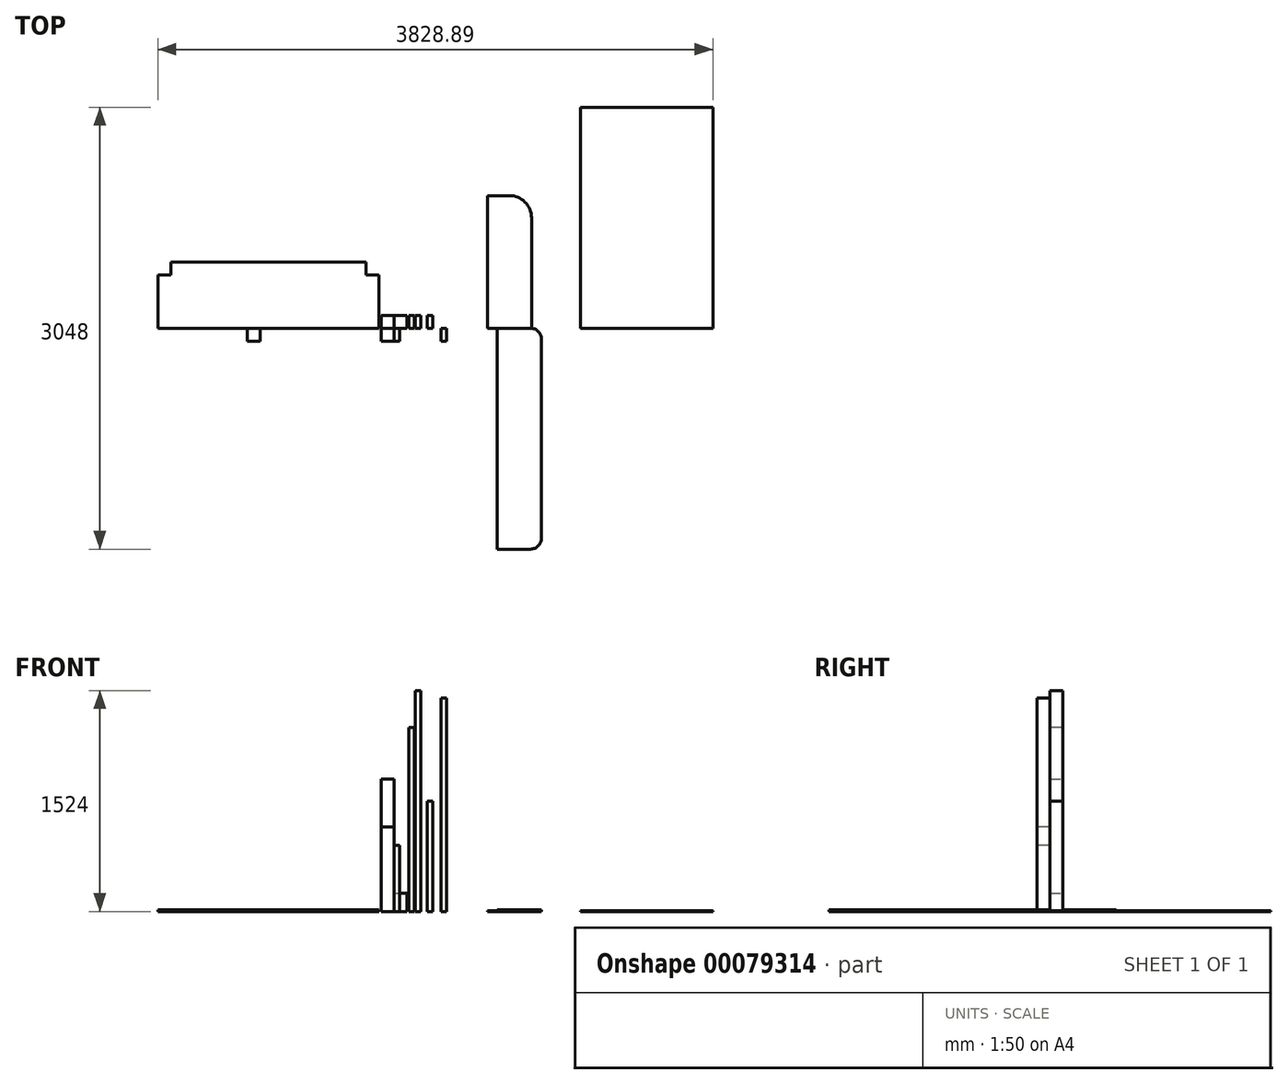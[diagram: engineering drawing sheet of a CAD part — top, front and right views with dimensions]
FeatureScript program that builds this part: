
annotation { "Feature Type Name" : "Feature", "Feature Type Description" : "" }
export const myFeature = defineFeature(function(context is Context, id is Id, definition is map)
    precondition{}
    {
        {
            var Q0;
            Q0=qCreatedBy(makeId("Top.planeOp"),FACE);
            var sketch = newSketch(context, id + "F0", { "sketchPlane" : qUnion([Q0])});
            skLineSegment(sketch, "E0.bottom", {"start": v(0, 0) * mm, "end": v(38.1, 0) * mm});
            skLineSegment(sketch, "E0.top", {"start": v(0, -88.9) * mm, "end": v(38.1, -88.9) * mm});
            skLineSegment(sketch, "E0.left", {"start": v(0, 0) * mm, "end": v(0, -88.9) * mm});
            skLineSegment(sketch, "E0.right", {"start": v(38.1, 0) * mm, "end": v(38.1, -88.9) * mm});
            skSolve(sketch);
        }
        {
            var Q0;
            Q0=qCreatedBy(makeId("Top.planeOp"),FACE);
            var sketch = newSketch(context, id + "F1", { "sketchPlane" : qUnion([Q0])});
            skLineSegment(sketch, "E1.bottom", {"start": v(0, 0) * mm, "end": v(-88.9, 0) * mm});
            skLineSegment(sketch, "E1.top", {"start": v(0, 88.9) * mm, "end": v(-88.9, 88.9) * mm});
            skLineSegment(sketch, "E1.left", {"start": v(0, 0) * mm, "end": v(0, 88.9) * mm});
            skLineSegment(sketch, "E1.right", {"start": v(-88.9, 0) * mm, "end": v(-88.9, 88.9) * mm});
            skSolve(sketch);
        }
        {
            var Q0;
            Q0=makeQuery(id+"F0.imprint","IMPRINT",FACE,{"disambiguationData":[TD([[makeQuery(id+"F0.imprint","IMPRINT",EDGE,{"derivedFrom":sQuery(id+"F0.wireOp",EDGE,"E0.bottom")}),-1.0]])]});
            extrude(context, id + "F2", {"entities" : qUnion([Q0]), "depth" : 457.2 * mm});
        }
        {
            var Q0;
            Q0=makeQuery(id+"F1.imprint","IMPRINT",FACE,{"disambiguationData":[TD([[makeQuery(id+"F1.imprint","IMPRINT",EDGE,{"derivedFrom":sQuery(id+"F1.wireOp",EDGE,"E1.bottom")}),-1.0]])]});
            extrude(context, id + "F3", {"entities" : qUnion([Q0]), "depth" : 914.4 * mm});
        }
        {
            var Q0;
            Q0=qCreatedBy(makeId("Top.planeOp"),FACE);
            var sketch = newSketch(context, id + "F4", { "sketchPlane" : qUnion([Q0])});
            skLineSegment(sketch, "E2.bottom", {"start": v(0, 0) * mm, "end": v(88.9, 0) * mm});
            skLineSegment(sketch, "E2.top", {"start": v(0, 88.9) * mm, "end": v(88.9, 88.9) * mm});
            skLineSegment(sketch, "E2.left", {"start": v(0, 0) * mm, "end": v(0, 88.9) * mm});
            skLineSegment(sketch, "E2.right", {"start": v(88.9, 0) * mm, "end": v(88.9, 88.9) * mm});
            skSolve(sketch);
        }
        {
            var Q0;
            Q0=qCreatedBy(makeId("Top.planeOp"),FACE);
            var sketch = newSketch(context, id + "F5", { "sketchPlane" : qUnion([Q0])});
            skLineSegment(sketch, "E3.bottom", {"start": v(0, 0) * mm, "end": v(-88.9, 0) * mm});
            skLineSegment(sketch, "E3.top", {"start": v(0, -88.9) * mm, "end": v(-88.9, -88.9) * mm});
            skLineSegment(sketch, "E3.left", {"start": v(0, 0) * mm, "end": v(0, -88.9) * mm});
            skLineSegment(sketch, "E3.right", {"start": v(-88.9, 0) * mm, "end": v(-88.9, -88.9) * mm});
            skSolve(sketch);
        }
        {
            var Q0;
            Q0=makeQuery(id+"F4.imprint","IMPRINT",FACE,{"disambiguationData":[TD([[makeQuery(id+"F4.imprint","IMPRINT",EDGE,{"derivedFrom":sQuery(id+"F4.wireOp",EDGE,"E2.bottom")}),1.0]])]});
            extrude(context, id + "F6", {"entities" : qUnion([Q0]), "depth" : 127 * mm});
        }
        {
            var Q0;
            Q0=makeQuery(id+"F5.imprint","IMPRINT",FACE,{"disambiguationData":[TD([[makeQuery(id+"F5.imprint","IMPRINT",EDGE,{"derivedFrom":sQuery(id+"F5.wireOp",EDGE,"E3.bottom")}),1.0]])]});
            extrude(context, id + "F7", {"entities" : qUnion([Q0]), "depth" : 584.2 * mm});
        }
        {
            var Q0;
            Q0=qCreatedBy(makeId("Top.planeOp"),FACE);
            var sketch = newSketch(context, id + "F8", { "sketchPlane" : qUnion([Q0])});
            skLineSegment(sketch, "E4.bottom", {"start": v(140.51, 88.9) * mm, "end": v(102.41, 88.9) * mm});
            skLineSegment(sketch, "E4.top", {"start": v(140.51, 0) * mm, "end": v(102.41, 0) * mm});
            skLineSegment(sketch, "E4.left", {"start": v(140.51, 88.9) * mm, "end": v(140.51, 0) * mm});
            skLineSegment(sketch, "E4.right", {"start": v(102.41, 88.9) * mm, "end": v(102.41, 0) * mm});
            skSolve(sketch);
        }
        {
            var Q0;
            Q0=makeQuery(id+"F8.imprint","IMPRINT",FACE,{"disambiguationData":[TD([[makeQuery(id+"F8.imprint","IMPRINT",EDGE,{"derivedFrom":sQuery(id+"F8.wireOp",EDGE,"E4.bottom")}),1.0]])]});
            extrude(context, id + "F9", {"entities" : qUnion([Q0]), "depth" : 1270 * mm});
        }
        {
            var Q0;
            Q0=qCreatedBy(makeId("Top.planeOp"),FACE);
            var sketch = newSketch(context, id + "F10", { "sketchPlane" : qUnion([Q0])});
            skLineSegment(sketch, "E5.bottom", {"start": v(183.48, 0) * mm, "end": v(145.38, 0) * mm});
            skLineSegment(sketch, "E5.top", {"start": v(183.48, 88.9) * mm, "end": v(145.38, 88.9) * mm});
            skLineSegment(sketch, "E5.left", {"start": v(183.48, 0) * mm, "end": v(183.48, 88.9) * mm});
            skLineSegment(sketch, "E5.right", {"start": v(145.38, 0) * mm, "end": v(145.38, 88.9) * mm});
            skSolve(sketch);
        }
        {
            var Q0;
            Q0=makeQuery(id+"F10.imprint","IMPRINT",FACE,{"disambiguationData":[TD([[makeQuery(id+"F10.imprint","IMPRINT",EDGE,{"derivedFrom":sQuery(id+"F10.wireOp",EDGE,"E5.bottom")}),-1.0]])]});
            extrude(context, id + "F11", {"entities" : qUnion([Q0]), "depth" : 1524 * mm});
        }
        {
            var Q0;
            Q0=qCreatedBy(makeId("Top.planeOp"),FACE);
            var sketch = newSketch(context, id + "F12", { "sketchPlane" : qUnion([Q0])});
            skLineSegment(sketch, "E6.bottom", {"start": v(267.37, 88.9) * mm, "end": v(229.27, 88.9) * mm});
            skLineSegment(sketch, "E6.top", {"start": v(267.37, 0) * mm, "end": v(229.27, 0) * mm});
            skLineSegment(sketch, "E6.left", {"start": v(267.37, 88.9) * mm, "end": v(267.37, 0) * mm});
            skLineSegment(sketch, "E6.right", {"start": v(229.27, 88.9) * mm, "end": v(229.27, 0) * mm});
            skSolve(sketch);
        }
        {
            var Q0;
            Q0=makeQuery(id+"F12.imprint","IMPRINT",FACE,{"disambiguationData":[TD([[makeQuery(id+"F12.imprint","IMPRINT",EDGE,{"derivedFrom":sQuery(id+"F12.wireOp",EDGE,"E6.bottom")}),1.0]])]});
            extrude(context, id + "F13", {"entities" : qUnion([Q0]), "depth" : 762 * mm});
        }
        {
            var Q0;
            Q0=qCreatedBy(makeId("Top.planeOp"),FACE);
            var sketch = newSketch(context, id + "F14", { "sketchPlane" : qUnion([Q0])});
            skLineSegment(sketch, "E7.bottom", {"start": v(-106.42, 0) * mm, "end": v(-1630.42, 0) * mm});
            skLineSegment(sketch, "E7.top", {"start": v(-106.42, 457.2) * mm, "end": v(-1630.42, 457.2) * mm});
            skLineSegment(sketch, "E7.left", {"start": v(-106.42, 0) * mm, "end": v(-106.42, 457.2) * mm});
            skLineSegment(sketch, "E7.right", {"start": v(-1630.42, 0) * mm, "end": v(-1630.42, 457.2) * mm});
            skLineSegment(sketch, "E8.bottom", {"start": v(-106.42, 457.2) * mm, "end": v(-195.32, 457.2) * mm});
            skLineSegment(sketch, "E8.top", {"start": v(-106.42, 368.3) * mm, "end": v(-195.32, 368.3) * mm});
            skLineSegment(sketch, "E8.left", {"start": v(-106.42, 457.2) * mm, "end": v(-106.42, 368.3) * mm});
            skLineSegment(sketch, "E8.right", {"start": v(-195.32, 457.2) * mm, "end": v(-195.32, 368.3) * mm});
            skLineSegment(sketch, "E9.top", {"start": v(-1630.42, 368.3) * mm, "end": v(-1541.52, 368.3) * mm});
            skLineSegment(sketch, "E9.left", {"start": v(-1630.42, 457.2) * mm, "end": v(-1630.42, 368.3) * mm});
            skLineSegment(sketch, "E9.right", {"start": v(-1541.52, 457.2) * mm, "end": v(-1541.52, 368.3) * mm});
            skSolve(sketch);
        }
        {
            var Q0;
            Q0=makeQuery(id+"F14.imprint","IMPRINT",FACE,{"disambiguationData":[TD([[makeQuery(id+"F14.imprint","IMPRINT",EDGE,{"derivedFrom":sQuery(id+"F14.wireOp",EDGE,"E7.bottom")}),-1.0]])]});
            extrude(context, id + "F15", {"entities" : qUnion([Q0]), "depth" : 12.7 * mm});
        }
        {
            var Q0;
            Q0=qCreatedBy(makeId("Top.planeOp"),FACE);
            var sketch = newSketch(context, id + "F16", { "sketchPlane" : qUnion([Q0])});
            skLineSegment(sketch, "E10.bottom", {"start": v(-125.56, 0) * mm, "end": v(-1014.56, 0) * mm});
            skLineSegment(sketch, "E10.top", {"start": v(-125.56, -457.2) * mm, "end": v(-1014.56, -457.2) * mm});
            skLineSegment(sketch, "E10.left", {"start": v(-125.56, 0) * mm, "end": v(-125.56, -457.2) * mm});
            skLineSegment(sketch, "E10.right", {"start": v(-1014.56, 0) * mm, "end": v(-1014.56, -457.2) * mm});
            skLineSegment(sketch, "E11.bottom", {"start": v(-1014.56, 0) * mm, "end": v(-925.66, 0) * mm});
            skLineSegment(sketch, "E11.top", {"start": v(-1014.56, -88.9) * mm, "end": v(-925.66, -88.9) * mm});
            skLineSegment(sketch, "E11.left", {"start": v(-1014.56, 0) * mm, "end": v(-1014.56, -88.9) * mm});
            skLineSegment(sketch, "E11.right", {"start": v(-925.66, 0) * mm, "end": v(-925.66, -88.9) * mm});
            skLineSegment(sketch, "E12.bottom", {"start": v(-1014.56, -457.2) * mm, "end": v(-925.66, -457.2) * mm});
            skLineSegment(sketch, "E12.top", {"start": v(-1014.56, -368.3) * mm, "end": v(-925.66, -368.3) * mm});
            skLineSegment(sketch, "E12.left", {"start": v(-1014.56, -457.2) * mm, "end": v(-1014.56, -368.3) * mm});
            skLineSegment(sketch, "E12.right", {"start": v(-925.66, -457.2) * mm, "end": v(-925.66, -368.3) * mm});
            skSolve(sketch);
        }
        {
            var Q0;
            Q0=makeQuery(id+"F16.imprint","IMPRINT",FACE,{"disambiguationData":[TD([[makeQuery(id+"F16.imprint","IMPRINT",EDGE,{"derivedFrom":sQuery(id+"F16.wireOp",EDGE,"E10.bottom")}),1.0]])]});
            extrude(context, id + "F17", {"entities" : qUnion([Q0]), "depth" : 12.7 * mm});
        }
        {
            var Q0;
            Q0=qCreatedBy(makeId("Top.planeOp"),FACE);
            var sketch = newSketch(context, id + "F18", { "sketchPlane" : qUnion([Q0])});
            skLineSegment(sketch, "E13.bottom", {"start": v(939.93, 0) * mm, "end": v(711.33, 0) * mm});
            skLineSegment(sketch, "E13.top", {"start": v(939.93, -1524) * mm, "end": v(711.33, -1524) * mm});
            skLineSegment(sketch, "E13.left", {"start": v(1016.13, -76.2) * mm, "end": v(1016.13, -1447.8) * mm});
            skLineSegment(sketch, "E13.right", {"start": v(711.33, 0) * mm, "end": v(711.33, -1524) * mm});
            skPoint(sketch, "E14.visualSharp", {"position": v(1016.13, 0) * mm});
            skArc(sketch, "E14.filletArc", {"start": v(1016.13, -76.2) * mm, "mid": v(993.82, -22.32) * mm, "end": v(939.93, 0) * mm});
            skPoint(sketch, "E15.visualSharp", {"position": v(1016.13, -1524) * mm});
            skArc(sketch, "E15.filletArc", {"start": v(939.93, -1524) * mm, "mid": v(993.82, -1501.68) * mm, "end": v(1016.13, -1447.8) * mm});
            skSolve(sketch);
        }
        {
            var Q0;
            Q0=makeQuery(id+"F18.imprint","IMPRINT",FACE,{"disambiguationData":[TD([[makeQuery(id+"F18.imprint","IMPRINT",EDGE,{"derivedFrom":sQuery(id+"F18.wireOp",EDGE,"E13.bottom")}),1.0]])]});
            extrude(context, id + "F19", {"entities" : qUnion([Q0]), "depth" : 12.7 * mm});
        }
        {
            var Q0;
            Q0=qCreatedBy(makeId("Top.planeOp"),FACE);
            var sketch = newSketch(context, id + "F20", { "sketchPlane" : qUnion([Q0])});
            skLineSegment(sketch, "E16.bottom", {"start": v(642.44, 0) * mm, "end": v(947.24, 0) * mm});
            skLineSegment(sketch, "E16.top", {"start": v(642.44, 914.4) * mm, "end": v(794.84, 914.4) * mm});
            skLineSegment(sketch, "E16.left", {"start": v(642.44, 0) * mm, "end": v(642.44, 914.4) * mm});
            skLineSegment(sketch, "E16.right", {"start": v(947.24, 0) * mm, "end": v(947.24, 762) * mm});
            skPoint(sketch, "E17.visualSharp", {"position": v(947.24, 914.4) * mm});
            skArc(sketch, "E17.filletArc", {"start": v(947.24, 762) * mm, "mid": v(902.6, 869.76) * mm, "end": v(794.84, 914.4) * mm});
            skSolve(sketch);
        }
        {
            var Q0;
            Q0=makeQuery(id+"F20.imprint","IMPRINT",FACE,{"disambiguationData":[TD([[makeQuery(id+"F20.imprint","IMPRINT",EDGE,{"derivedFrom":sQuery(id+"F20.wireOp",EDGE,"E16.bottom")}),1.0]])]});
            extrude(context, id + "F21", {"entities" : qUnion([Q0]), "depth" : 6.35 * mm});
        }
        {
            var Q0;
            Q0=qCreatedBy(makeId("Top.planeOp"),FACE);
            var sketch = newSketch(context, id + "F22", { "sketchPlane" : qUnion([Q0])});
            skLineSegment(sketch, "E18.bottom", {"start": v(1284.07, 0) * mm, "end": v(2198.47, 0) * mm});
            skLineSegment(sketch, "E18.top", {"start": v(1284.07, 1524) * mm, "end": v(2198.47, 1524) * mm});
            skLineSegment(sketch, "E18.left", {"start": v(1284.07, 0) * mm, "end": v(1284.07, 1524) * mm});
            skLineSegment(sketch, "E18.right", {"start": v(2198.47, 0) * mm, "end": v(2198.47, 1524) * mm});
            skSolve(sketch);
        }
        {
            var Q0;
            Q0=makeQuery(id+"F22.imprint","IMPRINT",FACE,{"disambiguationData":[TD([[makeQuery(id+"F22.imprint","IMPRINT",EDGE,{"derivedFrom":sQuery(id+"F22.wireOp",EDGE,"E18.bottom")}),1.0]])]});
            extrude(context, id + "F23", {"entities" : qUnion([Q0]), "depth" : 6.35 * mm});
        }
        {
            var Q0;
            Q0=qCreatedBy(makeId("Top.planeOp"),FACE);
            var sketch = newSketch(context, id + "F24", { "sketchPlane" : qUnion([Q0])});
            skLineSegment(sketch, "E19.bottom", {"start": v(324.77, 0) * mm, "end": v(362.87, 0) * mm});
            skLineSegment(sketch, "E19.top", {"start": v(324.77, -88.9) * mm, "end": v(362.87, -88.9) * mm});
            skLineSegment(sketch, "E19.left", {"start": v(324.77, 0) * mm, "end": v(324.77, -88.9) * mm});
            skLineSegment(sketch, "E19.right", {"start": v(362.87, 0) * mm, "end": v(362.87, -88.9) * mm});
            skSolve(sketch);
        }
        {
            var Q0;
            Q0=makeQuery(id+"F24.imprint","IMPRINT",FACE,{"disambiguationData":[TD([[makeQuery(id+"F24.imprint","IMPRINT",EDGE,{"derivedFrom":sQuery(id+"F24.wireOp",EDGE,"E19.bottom")}),-1.0]])]});
            extrude(context, id + "F25", {"entities" : qUnion([Q0]), "depth" : 1473.2 * mm});
        }
    });
